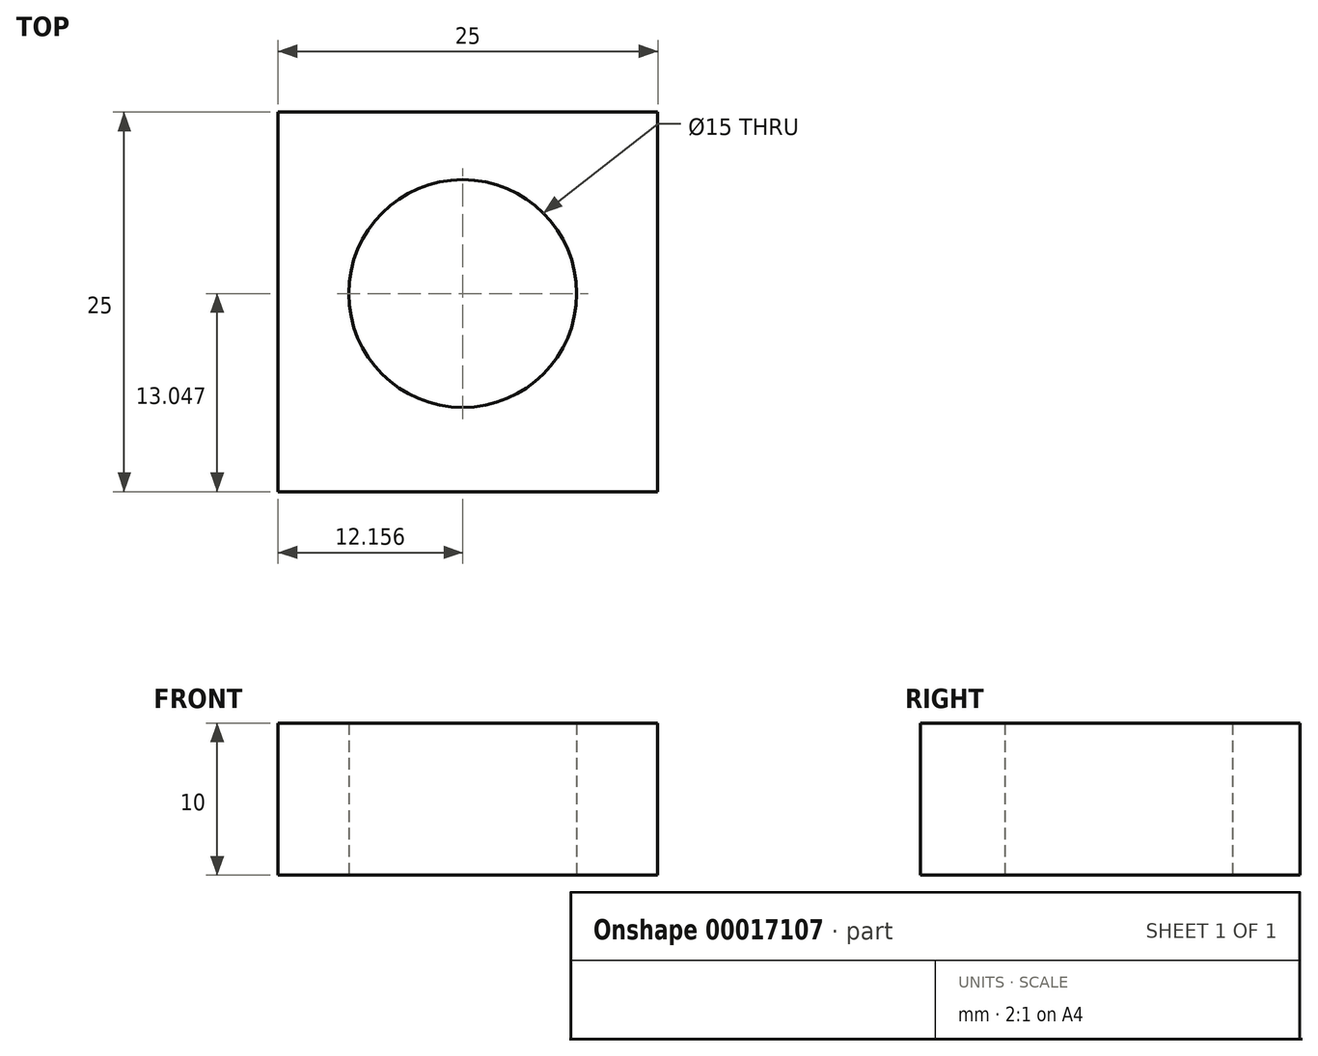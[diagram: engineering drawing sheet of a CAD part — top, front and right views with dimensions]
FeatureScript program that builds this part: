
annotation { "Feature Type Name" : "Feature", "Feature Type Description" : "" }
export const myFeature = defineFeature(function(context is Context, id is Id, definition is map)
    precondition{}
    {
        {
            var Q0;
            Q0=qCreatedBy(makeId("Top.planeOp"),FACE);
            var sketch = newSketch(context, id + "F0", { "sketchPlane" : qUnion([Q0])});
            skLineSegment(sketch, "E0.bottom", {"start": v(-14.42, 7.63) * mm, "end": v(10.58, 7.63) * mm});
            skLineSegment(sketch, "E0.top", {"start": v(-14.42, -17.37) * mm, "end": v(10.58, -17.37) * mm});
            skLineSegment(sketch, "E0.left", {"start": v(-14.42, 7.63) * mm, "end": v(-14.42, -17.37) * mm});
            skLineSegment(sketch, "E0.right", {"start": v(10.58, 7.63) * mm, "end": v(10.58, -17.37) * mm});
            skSolve(sketch);
        }
        {
            var Q0;
            Q0=makeQuery(id+"F0.imprint","IMPRINT",FACE,{"disambiguationData":[TD([[makeQuery(id+"F0.imprint","IMPRINT",EDGE,{"derivedFrom":sQuery(id+"F0.wireOp",EDGE,"E0.bottom")}),-1.0]])]});
            extrude(context, id + "F1", {"entities" : qUnion([Q0]), "depth" : 10 * mm});
        }
        {
            var Q0;
            Q0=qCreatedBy(makeId("Top.planeOp"),FACE);
            var sketch = newSketch(context, id + "F2", { "sketchPlane" : qUnion([Q0])});
            skLineSegment(sketch, "E1", {"start": v(-2.26, -4.32) * mm, "end": v(-2.26, -6.77) * mm});
            skSolve(sketch);
        }
        {
            var Q0;
            Q0=sQuery(id+"F2.wireOp",VERTEX,"E1.start");
            var Q1;
            Q1=makeQuery(id+"F1.opExtrude","SWEPT_BODY",BODY,{"disambiguationData":[OSD([sQuery(id+"F0.wireOp",EDGE,"E0.bottom"),sQuery(id+"F0.wireOp",EDGE,"E0.top"),sQuery(id+"F0.wireOp",EDGE,"E0.left"),sQuery(id+"F0.wireOp",EDGE,"E0.right")])]});
            hole(context, id + "F3", {"style" : HoleStyle.SIMPLE, "holeDiameter" : 15 * mm, "endStyle" : HoleEndStyle.THROUGH, "oppositeDirection" : true, "locations" : qUnion([Q0]), "scope" : qUnion([Q1])});
        }
    });
